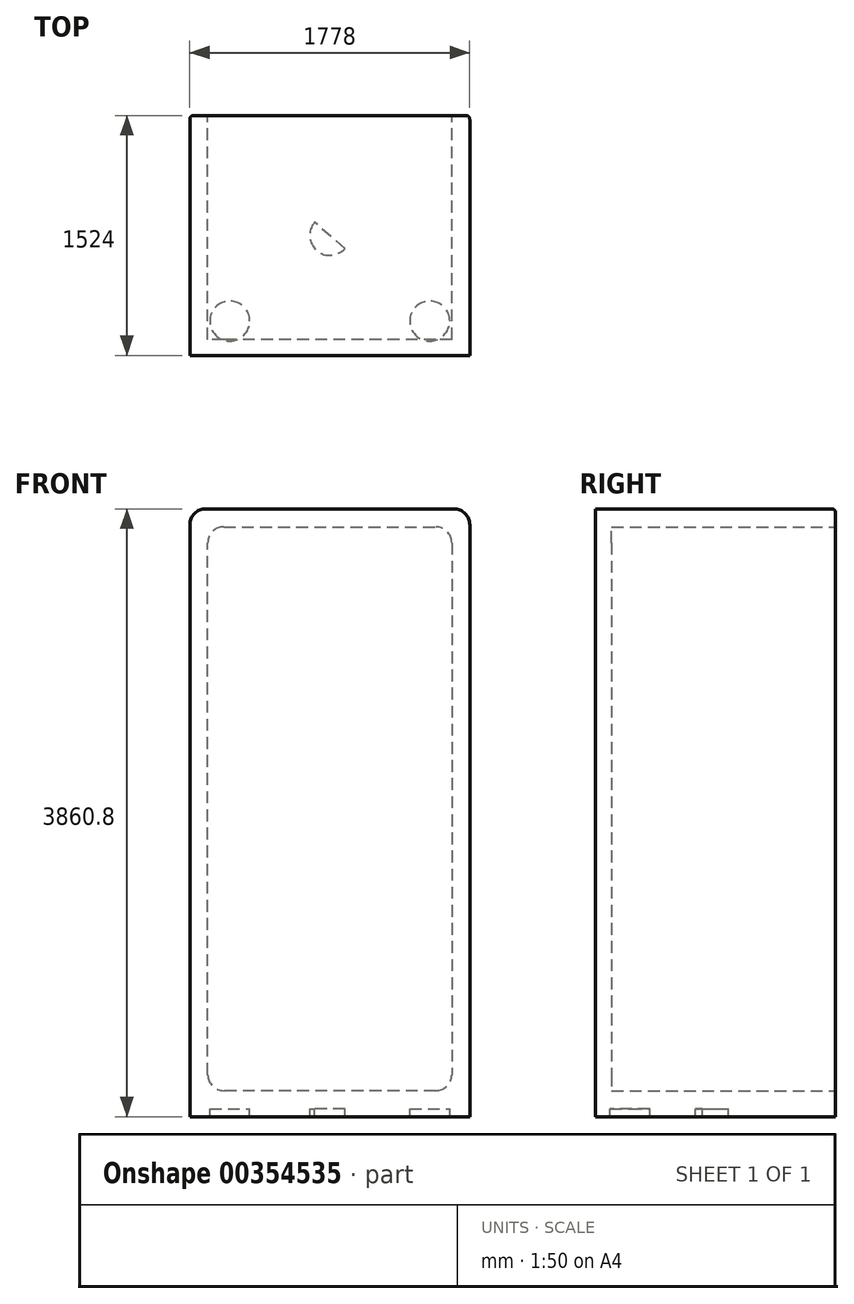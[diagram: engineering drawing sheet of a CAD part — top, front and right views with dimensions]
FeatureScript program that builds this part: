
annotation { "Feature Type Name" : "Feature", "Feature Type Description" : "" }
export const myFeature = defineFeature(function(context is Context, id is Id, definition is map)
    precondition{}
    {
        {
            var Q0;
            Q0=qCreatedBy(makeId("Top.planeOp"),FACE);
            var sketch = newSketch(context, id + "F0", { "sketchPlane" : qUnion([Q0])});
            skLineSegment(sketch, "E0.bottom", {"start": v(181.36, 0) * mm, "end": v(-1596.64, 0) * mm});
            skLineSegment(sketch, "E0.top", {"start": v(181.36, 1524) * mm, "end": v(-1596.64, 1524) * mm});
            skLineSegment(sketch, "E0.left", {"start": v(181.36, 0) * mm, "end": v(181.36, 1524) * mm});
            skLineSegment(sketch, "E0.right", {"start": v(-1596.64, 0) * mm, "end": v(-1596.64, 1524) * mm});
            skSolve(sketch);
        }
        {
            var Q0;
            Q0=makeQuery(id+"F0.imprint","IMPRINT",FACE,{"disambiguationData":[TD([[makeQuery(id+"F0.imprint","IMPRINT",EDGE,{"derivedFrom":sQuery(id+"F0.wireOp",EDGE,"E0.bottom")}),-1.0]])]});
            extrude(context, id + "F1", {"entities" : qUnion([Q0]), "depth" : 3810 * mm});
        }
        {
            var Q0;
            Q0=makeQuery(id+"F1.opExtrude","SWEPT_FACE",FACE,{"disambiguationData":[OSD([sQuery(id+"F0.wireOp",EDGE,"E0.top")])]});
            var sketch = newSketch(context, id + "F2", { "sketchPlane" : qUnion([Q0])});
            skLineSegment(sketch, "E1.0", {"start": v(-67.06, 114.3) * mm, "end": v(1482.34, 114.3) * mm});
            skLineSegment(sketch, "E1.1", {"start": v(-67.06, 3695.7) * mm, "end": v(-67.06, 114.3) * mm});
            skLineSegment(sketch, "E1.2", {"start": v(1482.34, 3695.7) * mm, "end": v(-67.06, 3695.7) * mm});
            skLineSegment(sketch, "E1.3", {"start": v(1482.34, 114.3) * mm, "end": v(1482.34, 3695.7) * mm});
            skSolve(sketch);
        }
        {
            var Q0;
            Q0=makeQuery(id+"F2.imprint","IMPRINT",FACE,{"disambiguationData":[TD([[makeQuery(id+"F2.imprint","IMPRINT",EDGE,{"derivedFrom":sQuery(id+"F2.wireOp",EDGE,"E1.0")}),1.0]])]});
            extrude(context, id + "F3", {"entities" : qUnion([Q0]), "operationType" : NewBodyOperationType.REMOVE, "oppositeDirection" : true, "depth" : 1422.4 * mm});
        }
        {
            var Q0;
            Q0=makeQuery(id+"F1.opExtrude","CAP_FACE",FACE,{"disambiguationData":[OSD([sQuery(id+"F0.wireOp",EDGE,"E0.bottom"),sQuery(id+"F0.wireOp",EDGE,"E0.top"),sQuery(id+"F0.wireOp",EDGE,"E0.left"),sQuery(id+"F0.wireOp",EDGE,"E0.right")])],"isStart":true});
            var sketch = newSketch(context, id + "F4", { "sketchPlane" : qUnion([Q0])});
            skLineSegment(sketch, "E2", {"start": v(-1596.64, 0) * mm, "end": v(181.36, -1524) * mm});
            skLineSegment(sketch, "E3", {"start": v(181.36, 0) * mm, "end": v(-1596.64, -1524) * mm});
            skCircle(sketch, "E4", {"center": v(-1342.64, -217.71) * mm, "radius": 127 * mm});
            skCircle(sketch, "E5", {"center": v(-72.64, -217.71) * mm, "radius": 127 * mm});
            skCircle(sketch, "E6", {"center": v(-72.64, -1306.29) * mm, "radius": 127 * mm});
            skCircle(sketch, "E7", {"center": v(-1342.64, -1306.29) * mm, "radius": 127 * mm});
            skCircle(sketch, "E8", {"center": v(-707.64, -762) * mm, "radius": 127 * mm});
            skSolve(sketch);
        }
        {
            var Q0;
            {var subQ0=sQuery(id+"F4.wireOp",EDGE,"E3");var subQ1=sQuery(id+"F4.wireOp",EDGE,"E2");var subQ2=makeQuery(id+"F4.imprint","INTERSECT",VERTEX,{"derivedFrom":[subQ1,subQ0]});Q0=makeQuery(id+"F4.imprint","IMPRINT",FACE,{"disambiguationData":[TD([[makeQuery(id+"F4.imprint","IMPRINT",EDGE,{"disambiguationData":[TD([[subQ2,-1.0]])],"derivedFrom":subQ1}),-1.0]])]});}
            var Q1;
            {var subQ0=sQuery(id+"F4.wireOp",EDGE,"E3");var subQ1=sQuery(id+"F4.wireOp",EDGE,"E2");var subQ2=makeQuery(id+"F4.imprint","INTERSECT",VERTEX,{"derivedFrom":[subQ1,subQ0]});Q1=makeQuery(id+"F4.imprint","IMPRINT",FACE,{"disambiguationData":[TD([[makeQuery(id+"F4.imprint","IMPRINT",EDGE,{"disambiguationData":[TD([[subQ2,-1.0]])],"derivedFrom":subQ1}),1.0]])]});}
            var Q2;
            {var subQ0=sQuery(id+"F4.wireOp",EDGE,"E8");var subQ1=sQuery(id+"F4.wireOp",EDGE,"E2");var subQ2=makeQuery(id+"F4.imprint","INTERSECT",VERTEX,{"disambiguationData":[OD(0.0)],"derivedFrom":[subQ1,subQ0]});Q2=makeQuery(id+"F4.imprint","IMPRINT",FACE,{"disambiguationData":[TD([[makeQuery(id+"F4.imprint","IMPRINT",EDGE,{"disambiguationData":[TD([[subQ2,-1.0]])],"derivedFrom":subQ1}),1.0]])]});}
            var Q3;
            {var subQ0=sQuery(id+"F4.wireOp",EDGE,"E8");var subQ1=sQuery(id+"F4.wireOp",EDGE,"E2");var subQ2=makeQuery(id+"F4.imprint","INTERSECT",VERTEX,{"disambiguationData":[OD(0.0)],"derivedFrom":[subQ1,subQ0]});Q3=makeQuery(id+"F4.imprint","IMPRINT",FACE,{"disambiguationData":[TD([[makeQuery(id+"F4.imprint","IMPRINT",EDGE,{"disambiguationData":[TD([[subQ2,-1.0]])],"derivedFrom":subQ1}),-1.0]])]});}
            var Q4;
            {var subQ0=sQuery(id+"F4.wireOp",EDGE,"E4");var subQ1=sQuery(id+"F4.wireOp",EDGE,"E2");var subQ2=makeQuery(id+"F4.imprint","INTERSECT",VERTEX,{"disambiguationData":[OD(0.0)],"derivedFrom":[subQ1,subQ0]});Q4=makeQuery(id+"F4.imprint","IMPRINT",FACE,{"disambiguationData":[TD([[makeQuery(id+"F4.imprint","IMPRINT",EDGE,{"disambiguationData":[TD([[subQ2,-1.0]])],"derivedFrom":subQ1}),-1.0]])]});}
            var Q5;
            {var subQ0=sQuery(id+"F4.wireOp",EDGE,"E4");var subQ1=sQuery(id+"F4.wireOp",EDGE,"E2");var subQ2=makeQuery(id+"F4.imprint","INTERSECT",VERTEX,{"disambiguationData":[OD(0.0)],"derivedFrom":[subQ1,subQ0]});Q5=makeQuery(id+"F4.imprint","IMPRINT",FACE,{"disambiguationData":[TD([[makeQuery(id+"F4.imprint","IMPRINT",EDGE,{"disambiguationData":[TD([[subQ2,-1.0]])],"derivedFrom":subQ1}),1.0]])]});}
            var Q6;
            {var subQ0=sQuery(id+"F4.wireOp",EDGE,"E5");var subQ1=sQuery(id+"F4.wireOp",EDGE,"E3");var subQ2=makeQuery(id+"F4.imprint","INTERSECT",VERTEX,{"disambiguationData":[OD(0.0)],"derivedFrom":[subQ1,subQ0]});Q6=makeQuery(id+"F4.imprint","IMPRINT",FACE,{"disambiguationData":[TD([[makeQuery(id+"F4.imprint","IMPRINT",EDGE,{"disambiguationData":[TD([[subQ2,-1.0]])],"derivedFrom":subQ1}),1.0]])]});}
            var Q7;
            {var subQ0=sQuery(id+"F4.wireOp",EDGE,"E5");var subQ1=sQuery(id+"F4.wireOp",EDGE,"E3");var subQ2=makeQuery(id+"F4.imprint","INTERSECT",VERTEX,{"disambiguationData":[OD(0.0)],"derivedFrom":[subQ1,subQ0]});Q7=makeQuery(id+"F4.imprint","IMPRINT",FACE,{"disambiguationData":[TD([[makeQuery(id+"F4.imprint","IMPRINT",EDGE,{"disambiguationData":[TD([[subQ2,-1.0]])],"derivedFrom":subQ1}),-1.0]])]});}
            var Q8;
            {var subQ0=sQuery(id+"F4.wireOp",EDGE,"E6");var subQ1=sQuery(id+"F4.wireOp",EDGE,"E2");var subQ2=makeQuery(id+"F4.imprint","INTERSECT",VERTEX,{"disambiguationData":[OD(0.0)],"derivedFrom":[subQ1,subQ0]});Q8=makeQuery(id+"F4.imprint","IMPRINT",FACE,{"disambiguationData":[TD([[makeQuery(id+"F4.imprint","IMPRINT",EDGE,{"disambiguationData":[TD([[subQ2,-1.0]])],"derivedFrom":subQ1}),1.0]])]});}
            var Q9;
            {var subQ0=sQuery(id+"F4.wireOp",EDGE,"E6");var subQ1=sQuery(id+"F4.wireOp",EDGE,"E2");var subQ2=makeQuery(id+"F4.imprint","INTERSECT",VERTEX,{"disambiguationData":[OD(0.0)],"derivedFrom":[subQ1,subQ0]});Q9=makeQuery(id+"F4.imprint","IMPRINT",FACE,{"disambiguationData":[TD([[makeQuery(id+"F4.imprint","IMPRINT",EDGE,{"disambiguationData":[TD([[subQ2,-1.0]])],"derivedFrom":subQ1}),-1.0]])]});}
            var Q10;
            {var subQ0=sQuery(id+"F4.wireOp",EDGE,"E7");var subQ1=sQuery(id+"F4.wireOp",EDGE,"E3");var subQ2=makeQuery(id+"F4.imprint","INTERSECT",VERTEX,{"disambiguationData":[OD(0.0)],"derivedFrom":[subQ1,subQ0]});Q10=makeQuery(id+"F4.imprint","IMPRINT",FACE,{"disambiguationData":[TD([[makeQuery(id+"F4.imprint","IMPRINT",EDGE,{"disambiguationData":[TD([[subQ2,-1.0]])],"derivedFrom":subQ1}),1.0]])]});}
            var Q11;
            {var subQ0=sQuery(id+"F4.wireOp",EDGE,"E7");var subQ1=sQuery(id+"F4.wireOp",EDGE,"E3");var subQ2=makeQuery(id+"F4.imprint","INTERSECT",VERTEX,{"disambiguationData":[OD(0.0)],"derivedFrom":[subQ1,subQ0]});Q11=makeQuery(id+"F4.imprint","IMPRINT",FACE,{"disambiguationData":[TD([[makeQuery(id+"F4.imprint","IMPRINT",EDGE,{"disambiguationData":[TD([[subQ2,-1.0]])],"derivedFrom":subQ1}),-1.0]])]});}
            extrude(context, id + "F5", {"entities" : qUnion([Q0, Q1, Q2, Q3, Q4, Q5, Q6, Q7, Q8, Q9, Q10, Q11]), "operationType" : NewBodyOperationType.ADD, "depth" : 50.8 * mm});
        }
        {
            var Q0;
            Q0=makeQuery(id+"F1.opExtrude","CAP_EDGE",EDGE,{"disambiguationData":[OSD([sQuery(id+"F0.wireOp",EDGE,"E0.left")])],"isStart":true});
            var Q1;
            Q1=makeQuery(id+"F1.opExtrude","CAP_EDGE",EDGE,{"disambiguationData":[OSD([sQuery(id+"F0.wireOp",EDGE,"E0.right")])],"isStart":true});
            var Q2;
            Q2=makeQuery(id+"F1.opExtrude","CAP_EDGE",EDGE,{"disambiguationData":[OSD([sQuery(id+"F0.wireOp",EDGE,"E0.left")])],"isStart":false});
            var Q3;
            Q3=makeQuery(id+"F1.opExtrude","CAP_EDGE",EDGE,{"disambiguationData":[OSD([sQuery(id+"F0.wireOp",EDGE,"E0.right")])],"isStart":false});
            var Q4;
            Q4=makeQuery(id+"F3.boolean.opBoolean","COPY",EDGE,{"derivedFrom":makeQuery(id+"F3.opExtrude","SWEPT_EDGE",EDGE,{"disambiguationData":[OSD([sQuery(id+"F2.wireOp",EDGE,"E1.1"),sQuery(id+"F2.wireOp",EDGE,"E1.2")])]})});
            var Q5;
            Q5=makeQuery(id+"F3.boolean.opBoolean","COPY",EDGE,{"derivedFrom":makeQuery(id+"F3.opExtrude","SWEPT_EDGE",EDGE,{"disambiguationData":[OSD([sQuery(id+"F2.wireOp",EDGE,"E1.2"),sQuery(id+"F2.wireOp",EDGE,"E1.3")])]})});
            var Q6;
            Q6=makeQuery(id+"F3.boolean.opBoolean","COPY",EDGE,{"derivedFrom":makeQuery(id+"F3.opExtrude","SWEPT_EDGE",EDGE,{"disambiguationData":[OSD([sQuery(id+"F2.wireOp",EDGE,"E1.0"),sQuery(id+"F2.wireOp",EDGE,"E1.3")])]})});
            var Q7;
            Q7=makeQuery(id+"F3.boolean.opBoolean","COPY",EDGE,{"derivedFrom":makeQuery(id+"F3.opExtrude","SWEPT_EDGE",EDGE,{"disambiguationData":[OSD([sQuery(id+"F2.wireOp",EDGE,"E1.0"),sQuery(id+"F2.wireOp",EDGE,"E1.1")])]})});
            fillet(context, id + "F6", {"entities" : qUnion([Q0, Q1, Q2, Q3, Q4, Q5, Q6, Q7]), "radius" : 101.6 * mm, "tangentPropagation" : true, "allowEdgeOverflow" : false});
        }
        {
            var Q0;
            Q0=makeQuery(id+"F1.opExtrude","SWEPT_EDGE",EDGE,{"disambiguationData":[OSD([sQuery(id+"F0.wireOp",EDGE,"E0.top"),sQuery(id+"F0.wireOp",EDGE,"E0.left")])]});
            fillet(context, id + "F7", {"entities" : qUnion([Q0]), "radius" : 25.4 * mm, "tangentPropagation" : true, "allowEdgeOverflow" : false});
        }
    });
